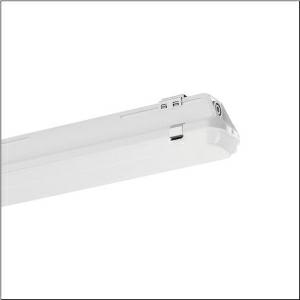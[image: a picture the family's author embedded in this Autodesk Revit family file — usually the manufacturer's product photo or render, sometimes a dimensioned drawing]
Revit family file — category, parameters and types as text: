
# Revit family: monsun_11_51fp12dp4b0u
name_source: partatom
category: Lighting Fixtures
units: mm (PartAtom-declared; Revit-internal decimal feet)

## family parameters
Cut with Voids When Loaded = No
Host = Face
Light Source = No
Part Type = Normal
Room Calculation Point = No
Round Connector Dimension = Use Diameter
Shared = No

## types (1)
- --- (1 x LED, 11850 lm, 63.5 W, 4000K)
    Apparent Load = 64 VA
    CIE Flux Codes = 62 86 96 97 100
    Color Rendering = 80
    Color Temperature = 4000K
    Default Elevation = 1800 mm
    Description = Monsun 11, damp-proof luminaire, chain hanger, primary light control with lens, primary optical cover: enclosure, of PMMA, light emission: direct distribution, primary light characteristic: symmetric, installation type: suspended mounting, surface-mounted, horizontal mounting, vertical mounting, LED, rated luminous flux: 11.850lm, luminous efficacy: 187lm/W, light colour: 840, colour temperature: 4000K, control gear: DALI 2, with terminal, 5-pole, max. 2.5mm², mains connection: 220..240V, AC, 50/60Hz, rated input power: 64W, luminaire housing, of glass-fibre reinforced polyester, uncoated, bright grey, incl. chain hanger, length: 1.590mm, width: 90mm, height: 88mm, clip for enclosure, of stainless steel (V2A), ceiling mounting element, of stainless steel (V2A), chain hanger, of stainless steel (V2A), protection rating (complete): IP66, insulation class (complete): insulation class I (protective earthing), certification: CE, ENEC, VDE, UKCA, protection symbol: D, impact resistance: IK04, permissible operating ambient temperature: -40..+35°C, standard: EN 50419, EN 60598-2-1, corresponds to IFS (International Featured Standards) requirements for safety and quality in the food industry, for indoor or canopied outdoor use, no direct snow, no direct sun, no direct rain, LABS conformity tested according to VDMA 24364:2018-05, contact your sales advisor before using the luminaires in applications with unclear chemical exposure, large temperature fluctuations or condensation-forming humidity, packaging unit: 1 piece
    Height = 89 mm
    Lamp = 1 x LED
    Lamp Light Flux = 11850 lm
    Lamp Power = 63.5 W
    Lamp count = 1
    Length = 1590 mm
    Luminous efficacy = 187 lm/W
    Manufacturer = Siteco
    ModVariant = No
    Model = 51FP12DP4B0U
    Mounting Place = Ceiling
    Mounting Type = Surface mounted
    Number of Poles = 1
    OnlyDefault = Yes
    Power Factor = 1
    Product Name = Monsun 11
    Product group = damp-proof luminaire
    ProductGroupID = 300
    Protection Class = Protection class I
    Protection Degree = IP 66
    RLX_Detail_Level = 1
    RLX_Emergency_Light_Flux = 0 lm
    RLX_Emergency_Type = 0
    RLX_Emergency_Type_DB = No
    RlxData = <blob elided: 92097 chars, md5=43464c77>
    Socket = socket
    Standby Power = 0 W
    System Light Flux = 11850 lm
    System Power = 64 W
    Type Comments = factory setting: luminous flux: 100 % | dim-lin: 254 | 439 mA
    Type Image = l_1349237.jpg
    URL = http://relux.com
    VarID = @adj_037849
    Voltage = 0 V
    Weight = 0.00 kg
    Width = 90 mm

## geometry (parser evidence)
native form markers: Blend x4, Sweep x10
no freeform markers — native parametric forms only
